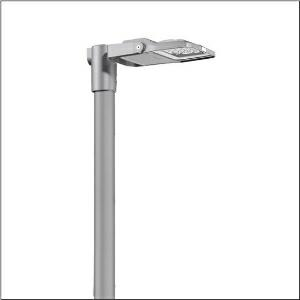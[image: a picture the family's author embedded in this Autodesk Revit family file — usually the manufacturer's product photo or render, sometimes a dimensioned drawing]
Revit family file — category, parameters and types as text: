
# Revit family: floodlight_fl_21_iq_micro___pl61_5xa7762a2c3a_d37b
name_source: partatom
category: Lighting Fixtures
units: mm (PartAtom-declared; Revit-internal decimal feet)

## family parameters
Cut with Voids When Loaded = No
Host = Face
Light Source = No
Part Type = Normal
Room Calculation Point = No
Round Connector Dimension = Use Diameter
Shared = No

## types (1)
- --- (1 x LED, 2910 lm, 23.1 W, 3000K)
    Apparent Load = 23 VA
    CIE Flux Codes = 33 65 98 100 100
    Color Rendering = 70
    Color Temperature = 3000K
    Default Elevation = 1800 mm
    Description = Floodlight FL 21 iQ micro, floodlight, primary light control with lens, of PMMA, primary optical cover: protective disc, of toughened safety glass, transparent, light distribution: PL61, light emission: direct distribution, installation type: surface-mounted, LED, High Power LED, rated luminous flux: 2.910lm, luminous efficacy: 126lm/W, light colour: 730, colour temperature: 3000K, control gear: iQ Street-Remote/DALI, control: Auto-Match, Temp-Guard, Night-Set, Smart-Wire, Desk-Remote (wireless, voltage-free reading and setting of iQ features in the workshop via application-optimized NFC function/RFID function), optimised constant luminous flux control (CLO 2.0), Street-Remote, with terminal, 6-pole, mains connection: 220..240V, AC, 50/60Hz, start of lifetime: 23W, end of service life: 24W, reduction: 11W, luminaire housing, of diecast aluminium, powder-coated, Siteco® metallic grey (DB 702S), corrosivity category C5 mid according to DIN EN ISO 12944, suitable for swimming pools, chlorine-resistant, sealing non-destructively replaceable, please order mast flange separately, mast bracket, of steel, galvanised, powder-coated, Siteco® metallic grey (DB 702S), protection rating (complete): IP66, insulation class (complete): insulation class II (safety insulation), certification: CE, ENEC, VDE, protection symbol: D, impact resistance: IK07, permissible operating ambient temperature: -40..+40°C, permissible operating ambient temperature for outdoor applications: -40..+50°C, standard: DIN EN 12944, LABS conformity tested according to VDMA 24364:2018-05, packaging unit: 1 piece

Light Distribution: PL61
    Height = 65 mm
    Lamp = 1 x LED
    Lamp Light Flux = 2910 lm
    Lamp Power = 23.1 W
    Lamp count = 1
    Length = 312 mm
    Luminous efficacy = 126 lm/W
    Manufacturer = Siteco
    ModVariant = No
    Model = 5XA7762A2C3A
    Number of Poles = 1
    OnlyDefault = Yes
    Power Factor = 1
    Product Name = Floodlight FL 21 iQ micro | PL61
    Product group = floodlight | pylon annexe
    ProductGroupID = 6200
    Protection Class = Protection class II
    Protection Degree = IP 66
    RLX_Detail_Level = 1
    RLX_Emergency_Light_Flux = 0 lm
    RLX_Emergency_Type = 0
    RLX_Emergency_Type_DB = No
    RlxData = <blob elided: 101869 chars, md5=31ab752d>
    Socket = socket
    Standby Power = 0 W
    System Light Flux = 2910 lm
    System Power = 23 W
    Type Comments = factory setting: luminous flux: 100 % | dim-lin: 254 | 455 mA
    Type Image = l_1007121.jpg
    URL = http://relux.com
    VarID = @adj_194368
    Voltage = 0 V
    Weight = 0.00 kg
    Width = 230 mm

## geometry (parser evidence)
native form markers: Blend x4, Sweep x11
no freeform markers — native parametric forms only
